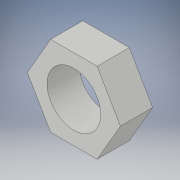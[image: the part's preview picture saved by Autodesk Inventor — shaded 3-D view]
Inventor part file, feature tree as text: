
AUTODESK INVENTOR PART (.ipt)
format: ipt  version: 2018 (Build 220112000, 112)  size: 100,864 bytes
history: native  units: in
note: dims shown in document units (in); Inventor stores cm internally (conversion verified against a paired STEP export)
features: extrude x1, sketch x1
ambient origin geometry x8: Origin, YZ Plane, XZ Plane, XY Plane, X Axis, Y Axis, Z Axis, Center Point
bodies: Solid1 (feature_tree)
feature tree (2):
  extrude  "Extrusion1"  Depth=0.375in
  sketch  "Sketch1"  dims[d0=0.9375in d1=0.625in d2=0.375in d3=0.0in]
